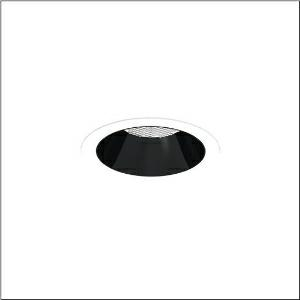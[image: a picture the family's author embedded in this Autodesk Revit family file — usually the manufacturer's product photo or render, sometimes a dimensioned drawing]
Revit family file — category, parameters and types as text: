
# Revit family: lunis_21_l_51db17ed91c
name_source: partatom
category: Lighting Fixtures
units: mm (PartAtom-declared; Revit-internal decimal feet)

## family parameters
Cut with Voids When Loaded = No
Host = Face
Light Source = No
Part Type = Normal
Room Calculation Point = No
Round Connector Dimension = Use Diameter
Shared = No

## types (1)
- --- (1 x LED, 3430 lm, 25.4 W, 6500K)
    Apparent Load = 25 VA
    CIE Flux Codes = 93 100 100 100 100
    Color Rendering = 80
    Color Temperature = 6500K
    Default Elevation = 1800 mm
    Description = Lunis 21,  L, downlight, light control with lens, of PMMA, anti glare with reflector, of PC, light emission: direct distribution, LED rated luminous flux: 1.790lm, light colour: 830/840/865, with terminal, 5-pole, mains connection: 220..240V, AC/DC, 0/50..60Hz, housing, round, of diecast aluminium, traffic white (RAL 9016), diameter: 165mm, clamping range: 1..40mm, protection rating (complete): IP20, protection rating (on room side): IP54, insulation class (complete): insulation class II (safety insulation), certification: CE, impact resistance: IK03, packaging unit: 1 piece
    Height = 0 mm  [stored 0 ft]
    Lamp = 1 x LED
    Lamp Light Flux = 3430 lm
    Lamp Power = 25.4 W
    Lamp count = 1
    Length = 165 mm
    Luminous efficacy = 135 lm/W
    Manufacturer = Siteco
    ModVariant = No
    Model = 51DB17ED91C
    Mounting Place = Ceiling
    Mounting Type = Recessed
    Number of Poles = 1
    OnlyDefault = Yes
    Power Factor = 1
    Product Name = Lunis 21 L
    Product group = downlight
    ProductGroupID = 400
    Protection Class = Protection class II
    Protection Degree = IP 20
    RLX_Detail_Level = 1
    RLX_Emergency_Light_Flux = 0 lm
    RLX_Emergency_Type = 0
    RLX_Emergency_Type_DB = No
    RlxData = <blob elided: 18521 chars, md5=8bc26458>
    Socket = socket
    Standby Power = 0 W
    System Light Flux = 3430 lm
    System Power = 25 W
    Type Comments = individual setting: colour temperature 6500K, luminous flux: 100 % | (ON | ON | OFF | OFF) | 700 mA
    Type Image = l_1291094.jpg
    URL = http://relux.com
    VarID = @adj_019902
    Voltage = 0 V
    Weight = 0.00 kg
    Width = 0 mm  [stored 0 ft]

note: [stored X ft] marks values corroborated as IEEE doubles in the binary element streams (Revit-internal decimal feet)

## geometry (parser evidence)
native form markers: Blend x4, Sweep x11
no freeform markers — native parametric forms only
